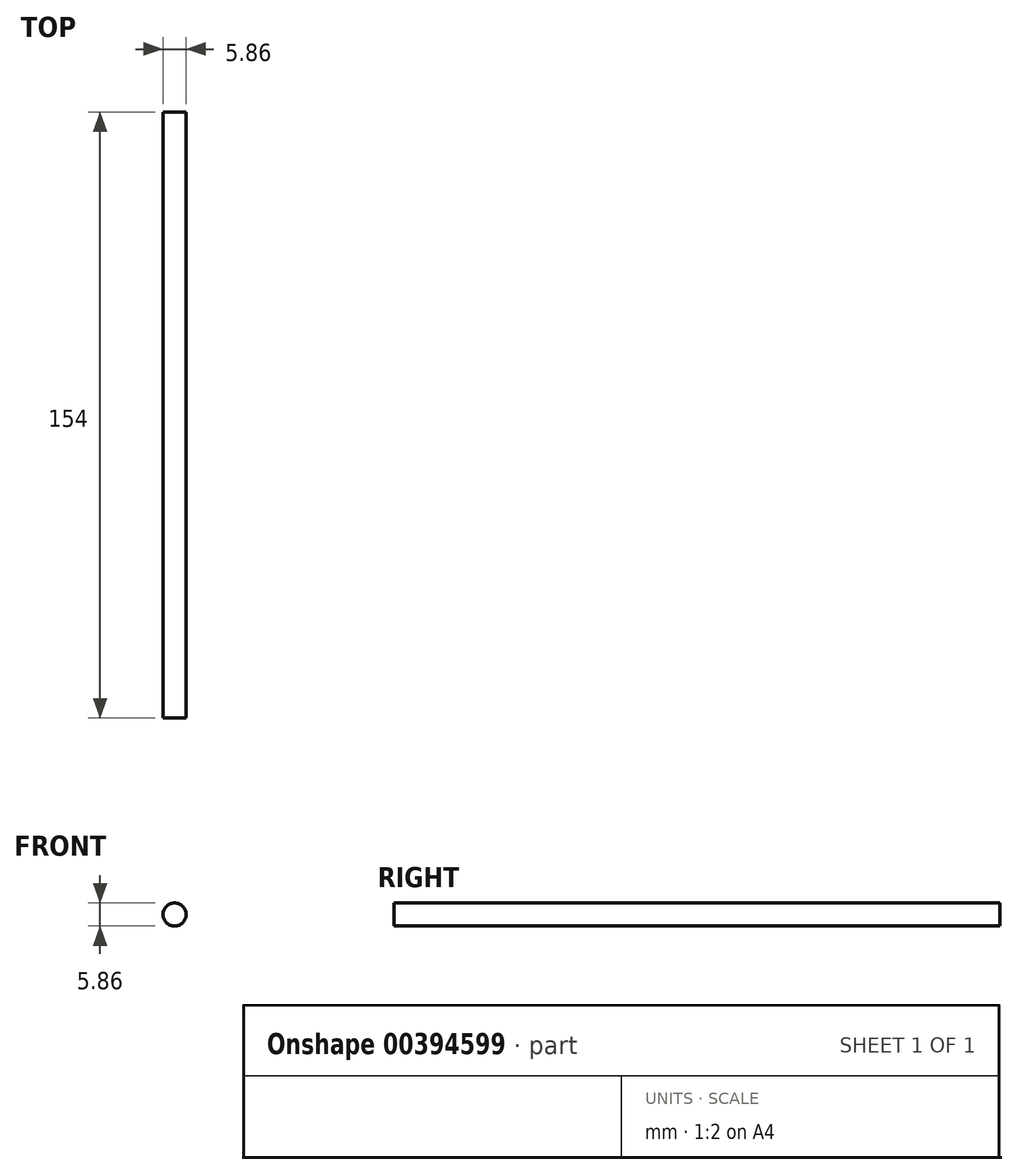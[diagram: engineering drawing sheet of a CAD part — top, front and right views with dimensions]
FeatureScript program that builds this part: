
annotation { "Feature Type Name" : "Feature", "Feature Type Description" : "" }
export const myFeature = defineFeature(function(context is Context, id is Id, definition is map)
    precondition{}
    {
        {
            var Q0;
            Q0=qCreatedBy(makeId("Front.planeOp"),FACE);
            var sketch = newSketch(context, id + "F0", { "sketchPlane" : qUnion([Q0])});
            skCircle(sketch, "E0", {"center": v(0, 0) * mm, "radius": 2.93 * mm});
            skSolve(sketch);
        }
        {
            var Q0;
            Q0 = qSketchRegion(id + "F0", true);
            extrude(context, id + "F1", {"entities" : qUnion([Q0]), "endBound" : BoundingType.SYMMETRIC, "depth" : 154 * mm});
        }
    });
